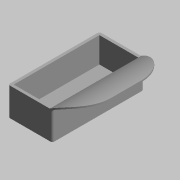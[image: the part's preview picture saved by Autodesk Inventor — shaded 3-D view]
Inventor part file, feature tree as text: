
AUTODESK INVENTOR PART (.ipt)
format: ipt  version: 2020 (Build 240168000, 168)  size: 141,824 bytes
history: native  units: mm (DEFAULTED — no unit token found)
features: extrude x3, sketch x3, fillet x2
ambient origin geometry x8: Origin, YZ Plane, XZ Plane, XY Plane, X Axis, Y Axis, Z Axis, Center Point
bodies: Solid1 (feature_tree)
feature tree (8):
  extrude  "Extrusion1"  Depth=97.0mm
  extrude  "Extrusion2"  Depth=48.5mm
  extrude  "Extrusion3"  Depth=32.0mm
  fillet  "Fillet2"  Radius=27.0mm
  fillet  "Fillet3"  Radius=30.0mm
  sketch  "Sketch1"  dims[d0=47.0mm d1=97.0mm]
  sketch  "Sketch2"  dims[d2=23.5mm d3=48.5mm]
  sketch  "Sketch4"  dims[d4=30.0mm d5=0.0mm d6=3.0mm d7=27.0mm d8=0.0mm d11=30.0mm d12=10.0mm d13=1.48221mm d14=10.0mm d15=0.0mm d16=2.0mm d17=32.0mm]
